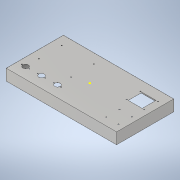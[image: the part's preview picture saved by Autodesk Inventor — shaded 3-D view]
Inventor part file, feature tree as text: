
AUTODESK INVENTOR PART (.ipt)
format: ipt  version: 2020 (Build 240168000, 168)  size: 218,112 bytes
history: native  units: mm
features: sketch x7, extrude x6
ambient origin geometry x8: Origin, YZ Plane, XZ Plane, XY Plane, X Axis, Y Axis, Z Axis, Center Point
bodies: Solid1 (feature_tree)
feature tree (13):
  extrude  "Extrusion1"  Depth=230.0mm
  extrude  "Extrusion6"  Depth=0.12mm
  extrude  "Extrusion7"  Depth=44.88mm TaperAngle=0.0deg
  extrude  "Extrusion8"  Depth=33.0mm
  extrude  "Extrusion9"  Depth=22.0mm
  extrude  "Extrusion10"  Depth=45.0mm
  sketch  "Sketch15"  dims[d36=4.0mm d37=15.0mm d38=4.0mm d39=15.0mm d40=4.0mm d41=4.0mm d42=4.0mm d43=4.0mm d44=15.0mm d45=15.0mm d46=15.0mm d47=15.0mm d50=129.25mm d52=39.45mm d54=32.4mm d55=91.7mm d56=4.0mm d57=4.0mm d58=4.0mm d59=4.0mm d60=4.0mm d61=0.0mm d65=22.5mm d66=40.65mm d67=56.0mm d68=4.2mm d69=4.2mm d70=4.2mm d71=4.2mm d72=70.5mm d73=0.0mm d74=0.0mm d75=49.7mm d77=53.4mm d79=30.5mm d80=4.2mm d81=4.2mm d82=4.2mm d83=4.2mm d84=0.0mm d85=0.0mm d86=56.0mm d87=56.0mm d88=7.1mm d89=7.1mm d90=7.1mm d92=15.0mm d94=7.1mm d95=4.0mm d96=0.0mm]
  sketch  "Sketch1"  dims[d0=444.0mm d1=230.0mm]
  sketch  "Sketch10"  dims[d2=45.0mm d3=0.0mm d19=0.12mm]
  sketch  "Sketch11"  dims[d20=0.12mm d21=44.88mm d22=0.0mm]
  sketch  "Sketch12"  dims[d24=22.0mm d25=33.0mm]
  sketch  "Sketch13"  dims[d27=22.0mm d30=64.0mm d31=22.0mm]
  sketch  "Sketch14"  dims[d33=64.0mm d35=45.0mm]
